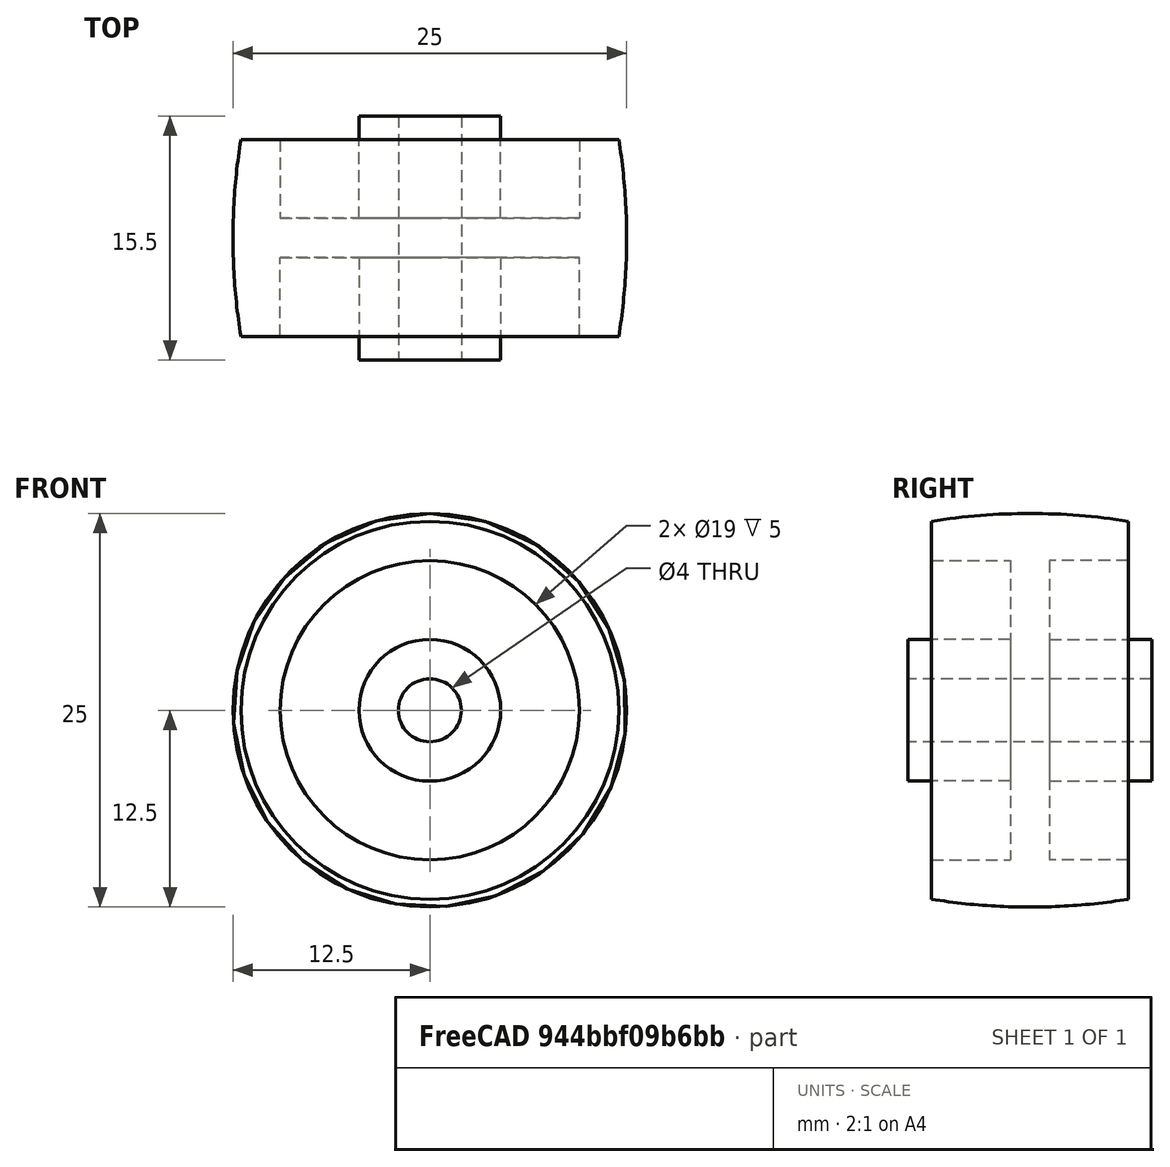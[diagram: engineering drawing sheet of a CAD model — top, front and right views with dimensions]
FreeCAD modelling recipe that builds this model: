
FCSTD DOCUMENT  (FreeCAD 1.0R39109 (Git))
Label: caster_wheel_p3
License: All rights reserved
LicenseURL: http://en.wikipedia.org/wiki/All_rights_reserved
objects: Sketcher::SketchObject×1, PartDesign::Revolution×1, PartDesign::Body×1
note: 6 computed .brp shape members not serialized (recipe doc carries the construction recipe); baked Part::Feature solids carry a one-line shape summary decoded from their .brp

FEATURE [Sketcher::SketchObject] Sketch
  ArcFitTolerance = 1e-06
  AttachmentSupport = -> [YZ_Plane]
  FullyConstrained = true
  MakeInternals = false
  MapMode = 5
  Placement = pos=(0,0,0) rot=(0.57735,0.57735,0.57735;2.0944rad)
  sketch-geometry (16):
    g0: ArcOfCircle CenterX=0 CenterY=-26.8125 CenterZ=0 NormalX=0 NormalY=0 NormalZ=1 AngleXU=0 Radius=39.3125 StartAngle=1.41114 EndAngle=1.5708
    g1: LineSegment [constr] StartX=2.1e-15 StartY=12.5 StartZ=0 EndX=-5 EndY=12.5 EndZ=0
    g2: LineSegment StartX=6.25 StartY=12 StartZ=0 EndX=6.25 EndY=9.5 EndZ=0
    g3: LineSegment StartX=6.25 StartY=9.5 StartZ=0 EndX=1.25 EndY=9.5 EndZ=0
    g4: LineSegment StartX=1.25 StartY=9.5 StartZ=0 EndX=1.25 EndY=4.5 EndZ=0
    g5: LineSegment StartX=1.25 StartY=4.5 StartZ=0 EndX=7.75 EndY=4.5 EndZ=0
    g6: LineSegment StartX=7.75 StartY=4.5 StartZ=0 EndX=7.75 EndY=2 EndZ=0
    g7: LineSegment StartX=0 StartY=2 StartZ=0 EndX=7.75 EndY=2 EndZ=0
    g8: LineSegment [constr] StartX=0 StartY=2 StartZ=0 EndX=2.1e-15 EndY=12.5 EndZ=0
    g9: ArcOfCircle CenterX=-5.54173e-05 CenterY=-26.8125 CenterZ=0 NormalX=0 NormalY=0 NormalZ=1 AngleXU=0 Radius=39.3125 StartAngle=1.57079 EndAngle=1.73045
    g10: LineSegment StartX=-6.25 StartY=12 StartZ=0 EndX=-6.25 EndY=9.5 EndZ=0
    g11: LineSegment StartX=-6.25 StartY=9.5 StartZ=0 EndX=-1.25 EndY=9.5 EndZ=0
    g12: LineSegment StartX=-1.25 StartY=9.5 StartZ=0 EndX=-1.25 EndY=4.5 EndZ=0
    g13: LineSegment StartX=-1.25 StartY=4.5 StartZ=0 EndX=-7.75 EndY=4.5 EndZ=0
    g14: LineSegment StartX=-7.75 StartY=4.5 StartZ=0 EndX=-7.75 EndY=2 EndZ=0
    g15: LineSegment StartX=0 StartY=2 StartZ=0 EndX=-7.75 EndY=2 EndZ=0
  constraints (48):
    c: PointOnObject(g0,g-2)
    c: Horizontal(g1)
    c: Tangent(g1,g0) = -1.5708
    c: DistanceY(g0) = 12.5
    c: Coincident(g2,g0)
    c: Vertical(g2)
    c: Coincident(g3,g2)
    c: Horizontal(g3)
    c: Coincident(g4,g3)
    c: Vertical(g4)
    c: Coincident(g5,g4)
    c: Horizontal(g5)
    c: Coincident(g6,g5)
    c: Vertical(g6)
    c: PointOnObject(g7,g-2)
    c: Coincident(g7,g6)
    c: Horizontal(g7)
    c: Coincident(g8,g7)
    c: Coincident(g8,g0)
    c: DistanceY(g-1,g6) = 2
    c: DistanceY(g6,g6) = 2.5
    c: DistanceY(g4,g4) = 5
    c: DistanceY(g2,g2) = 2.5
    c: DistanceX(g2,g5) = 1.5
    c: DistanceX(g3,g3) = 5
    c: DistanceX(g4) = 1.25
    c: DistanceX(g1) = -5
    c: Coincident(g10,g9)
    c: Coincident(g11,g10)
    c: Coincident(g12,g11)
    c: Coincident(g13,g12)
    c: Coincident(g14,g13)
    c: Coincident(g15,g14)
    c: Equal(g9,g0)
    c: Equal(g3,g11)
    c: Equal(g12,g4)
    c: Equal(g13,g5)
    c: Equal(g14,g6)
    c: Equal(g15,g7)
    c: Vertical(g10)
    c: Vertical(g12)
    c: Horizontal(g11)
    c: Tangent(g1,g9)
    c: Horizontal(g13)
    c: Vertical(g14)
    c: Horizontal(g15)
    c: Coincident(g15,g7)
    c: Coincident(g9,g0)
FEATURE [PartDesign::Revolution] Revolution  label="WheelRevolution"
  Angle = 360
  Angle2 = 60
  Axis = (0,1,0)
  Base = (0,0,0)
  Placement = pos=(0,0,0) rot=(1,1,1;2.0944rad)
  Profile = -> Sketch
  ReferenceAxis = -> Sketch [H_Axis]
  Refine = true
  Suppressed = false
  Type = 0
FEATURE [PartDesign::Body] Body  label="CasterWheelP3"
  AllowCompound = false
  Group = -> [Sketch,Revolution]
  Origin = -> Origin
  Tip = -> Revolution
